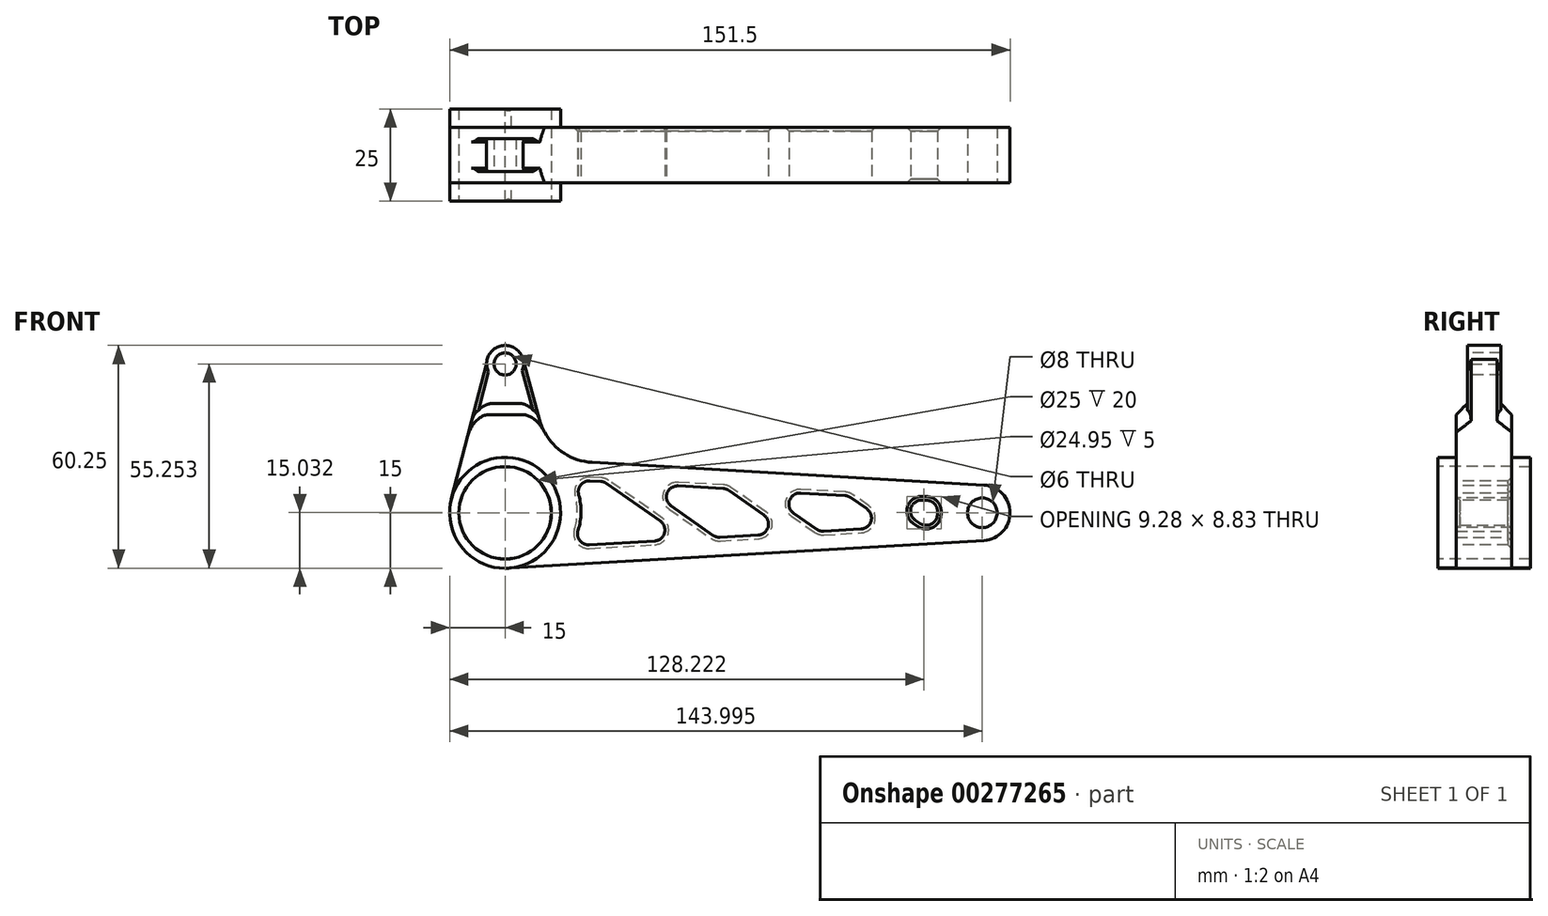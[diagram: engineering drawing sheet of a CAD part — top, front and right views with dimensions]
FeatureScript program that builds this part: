
annotation { "Feature Type Name" : "Feature", "Feature Type Description" : "" }
export const myFeature = defineFeature(function(context is Context, id is Id, definition is map)
    precondition{}
    {
        {
            var Q0;
            Q0=qCreatedBy(makeId("Front.planeOp"),FACE);
            var sketch = newSketch(context, id + "F0", { "sketchPlane" : qUnion([Q0])});
            skArc(sketch, "E0", {"start": v(129.43, -7.49) * mm, "mid": v(136.5, 0) * mm, "end": v(129.43, 7.49) * mm});
            skLineSegment(sketch, "E1", {"start": v(0, -15) * mm, "end": v(129.43, -7.49) * mm});
            skArc(sketch, "E2", {"start": v(4.84, 41.5) * mm, "mid": v(-0.62, 45.21) * mm, "end": v(-5, 40.25) * mm});
            skLineSegment(sketch, "E3", {"start": v(-5, 40.25) * mm, "end": v(-14.51, 3.79) * mm});
            skLineSegment(sketch, "E4", {"start": v(4.84, 41.5) * mm, "end": v(12.32, 14.29) * mm});
            skLineSegment(sketch, "E5.trimOffspring", {"start": v(12.32, 14.29) * mm, "end": v(129.43, 7.49) * mm});
            skPoint(sketch, "E6.start.orphan", {"position": v(0, 15) * mm});
            skArc(sketch, "E7.trimOffspring", {"start": v(-14.51, 3.79) * mm, "mid": v(-11.32, -9.84) * mm, "end": v(1.74, -14.9) * mm});
            skSolve(sketch);
        }
        {
            var Q0;
            {var subQ3=sQuery(id+"F0.wireOp",EDGE,"E0");Q0=makeQuery(id+"F0.imprint","IMPRINT",FACE,{"disambiguationData":[TD([[makeQuery(id+"F0.imprint","IMPRINT",EDGE,{"derivedFrom":subQ3}),1.0]])]});}
            extrude(context, id + "F1", {"entities" : qUnion([Q0]), "depth" : 15 * mm});
        }
        {
            var Q0;
            Q0=makeQuery(id+"F1.opExtrude","CAP_FACE",FACE,{"disambiguationData":[OSD([sQuery(id+"F0.wireOp",EDGE,"zeMrZWvo-Hzse-3JP0-Xgxd-alvhm16MrBRy"),sQuery(id+"F0.wireOp",EDGE,"E0"),sQuery(id+"F0.wireOp",EDGE,"E6"),sQuery(id+"F0.wireOp",EDGE,"E1")])],"isStart":false});
            var sketch = newSketch(context, id + "F2", { "sketchPlane" : qUnion([Q0])});
            skCircle(sketch, "E8", {"center": v(0, 0) * mm, "radius": 12.5 * mm});
            skCircle(sketch, "E9", {"center": v(129, 0) * mm, "radius": 4 * mm});
            skSolve(sketch);
        }
        {
            var Q0;
            Q0 = qSketchRegion(id + "F2", true);
            extrude(context, id + "F3", {"entities" : qUnion([Q0]), "operationType" : NewBodyOperationType.REMOVE, "endBound" : BoundingType.THROUGH_ALL, "oppositeDirection" : true, "depth" : 25 * mm});
        }
        {
            var Q0;
            Q0=makeQuery(id+"F1.opExtrude","CAP_FACE",FACE,{"disambiguationData":[OSD([sQuery(id+"F0.wireOp",EDGE,"zeMrZWvo-Hzse-3JP0-Xgxd-alvhm16MrBRy"),sQuery(id+"F0.wireOp",EDGE,"E0"),sQuery(id+"F0.wireOp",EDGE,"E6"),sQuery(id+"F0.wireOp",EDGE,"E1")])],"isStart":false});
            var sketch = newSketch(context, id + "F4", { "sketchPlane" : qUnion([Q0])});
            skLineSegment(sketch, "E10", {"start": v(18.1, 8.94) * mm, "end": v(26.69, 8.44) * mm});
            skLineSegment(sketch, "E11", {"start": v(17.63, -8.97) * mm, "end": v(49, -7.15) * mm});
            skArc(sketch, "E12", {"start": v(17.63, -8.97) * mm, "mid": v(20.5, -0.08) * mm, "end": v(18.1, 8.94) * mm});
            skArc(sketch, "E13", {"start": v(117.93, 3.15) * mm, "mid": v(116.86, 0.05) * mm, "end": v(117.46, -3.17) * mm});
            skLineSegment(sketch, "E14", {"start": v(26.69, 8.44) * mm, "end": v(49, -7.15) * mm});
            skLineSegment(sketch, "E15", {"start": v(36.2, 7.89) * mm, "end": v(57.06, -6.68) * mm});
            skLineSegment(sketch, "E16", {"start": v(59.79, 6.52) * mm, "end": v(77.02, -5.52) * mm});
            skLineSegment(sketch, "E17", {"start": v(69.3, 5.97) * mm, "end": v(85.08, -5.05) * mm});
            skLineSegment(sketch, "E18", {"start": v(92.66, 4.61) * mm, "end": v(104.85, -3.9) * mm});
            skLineSegment(sketch, "E19", {"start": v(102.18, 4.06) * mm, "end": v(112.91, -3.44) * mm});
            skLineSegment(sketch, "E20.trimOffspring", {"start": v(36.2, 7.89) * mm, "end": v(59.79, 6.52) * mm});
            skLineSegment(sketch, "E21.trimOffspring", {"start": v(57.06, -6.68) * mm, "end": v(77.02, -5.52) * mm});
            skLineSegment(sketch, "E22.trimOffspring", {"start": v(85.08, -5.05) * mm, "end": v(104.85, -3.9) * mm});
            skLineSegment(sketch, "E23.trimOffspring", {"start": v(69.3, 5.97) * mm, "end": v(92.66, 4.61) * mm});
            skLineSegment(sketch, "E24.trimOffspring", {"start": v(102.18, 4.06) * mm, "end": v(117.93, 3.15) * mm});
            skLineSegment(sketch, "E25.trimOffspring", {"start": v(112.91, -3.44) * mm, "end": v(117.46, -3.17) * mm});
            skSolve(sketch);
        }
        {
            var Q0;
            Q0 = qSketchRegion(id + "F4", true);
            extrude(context, id + "F5", {"entities" : qUnion([Q0]), "operationType" : NewBodyOperationType.REMOVE, "oppositeDirection" : true, "depth" : 25 * mm});
        }
        {
            var Q0;
            Q0=makeQuery(id+"F5.boolean.opBoolean","COPY",EDGE,{"derivedFrom":makeQuery(id+"F5.opExtrude","SWEPT_EDGE",EDGE,{"disambiguationData":[OSD([sQuery(id+"F4.wireOp",EDGE,"E10"),sQuery(id+"F4.wireOp",EDGE,"E12")])]})});
            var Q1;
            Q1=makeQuery(id+"F5.boolean.opBoolean","COPY",EDGE,{"derivedFrom":makeQuery(id+"F5.opExtrude","SWEPT_EDGE",EDGE,{"disambiguationData":[OSD([sQuery(id+"F4.wireOp",EDGE,"E11"),sQuery(id+"F4.wireOp",EDGE,"E12")])]})});
            var Q2;
            Q2=makeQuery(id+"F5.boolean.opBoolean","COPY",EDGE,{"derivedFrom":makeQuery(id+"F5.opExtrude","SWEPT_EDGE",EDGE,{"disambiguationData":[OSD([sQuery(id+"F4.wireOp",EDGE,"E10"),sQuery(id+"F4.wireOp",EDGE,"E14")])]})});
            var Q3;
            Q3=makeQuery(id+"F5.boolean.opBoolean","COPY",EDGE,{"derivedFrom":makeQuery(id+"F5.opExtrude","SWEPT_EDGE",EDGE,{"disambiguationData":[OSD([sQuery(id+"F4.wireOp",EDGE,"E11"),sQuery(id+"F4.wireOp",EDGE,"E14")])]})});
            var Q4;
            Q4=makeQuery(id+"F5.boolean.opBoolean","COPY",EDGE,{"derivedFrom":makeQuery(id+"F5.opExtrude","SWEPT_EDGE",EDGE,{"disambiguationData":[OSD([sQuery(id+"F4.wireOp",EDGE,"E15"),sQuery(id+"F4.wireOp",EDGE,"E21.trimOffspring")])]})});
            var Q5;
            Q5=makeQuery(id+"F5.boolean.opBoolean","COPY",EDGE,{"derivedFrom":makeQuery(id+"F5.opExtrude","SWEPT_EDGE",EDGE,{"disambiguationData":[OSD([sQuery(id+"F4.wireOp",EDGE,"E15"),sQuery(id+"F4.wireOp",EDGE,"E20.trimOffspring")])]})});
            var Q6;
            Q6=makeQuery(id+"F5.boolean.opBoolean","COPY",EDGE,{"derivedFrom":makeQuery(id+"F5.opExtrude","SWEPT_EDGE",EDGE,{"disambiguationData":[OSD([sQuery(id+"F4.wireOp",EDGE,"E16"),sQuery(id+"F4.wireOp",EDGE,"E20.trimOffspring")])]})});
            var Q7;
            Q7=makeQuery(id+"F5.boolean.opBoolean","COPY",EDGE,{"derivedFrom":makeQuery(id+"F5.opExtrude","SWEPT_EDGE",EDGE,{"disambiguationData":[OSD([sQuery(id+"F4.wireOp",EDGE,"E16"),sQuery(id+"F4.wireOp",EDGE,"E21.trimOffspring")])]})});
            var Q8;
            Q8=makeQuery(id+"F5.boolean.opBoolean","COPY",EDGE,{"derivedFrom":makeQuery(id+"F5.opExtrude","SWEPT_EDGE",EDGE,{"disambiguationData":[OSD([sQuery(id+"F4.wireOp",EDGE,"E17"),sQuery(id+"F4.wireOp",EDGE,"E23.trimOffspring")])]})});
            var Q9;
            Q9=makeQuery(id+"F5.boolean.opBoolean","COPY",EDGE,{"derivedFrom":makeQuery(id+"F5.opExtrude","SWEPT_EDGE",EDGE,{"disambiguationData":[OSD([sQuery(id+"F4.wireOp",EDGE,"E18"),sQuery(id+"F4.wireOp",EDGE,"E23.trimOffspring")])]})});
            var Q10;
            Q10=makeQuery(id+"F5.boolean.opBoolean","COPY",EDGE,{"derivedFrom":makeQuery(id+"F5.opExtrude","SWEPT_EDGE",EDGE,{"disambiguationData":[OSD([sQuery(id+"F4.wireOp",EDGE,"E18"),sQuery(id+"F4.wireOp",EDGE,"E22.trimOffspring")])]})});
            var Q11;
            Q11=makeQuery(id+"F5.boolean.opBoolean","COPY",EDGE,{"derivedFrom":makeQuery(id+"F5.opExtrude","SWEPT_EDGE",EDGE,{"disambiguationData":[OSD([sQuery(id+"F4.wireOp",EDGE,"E17"),sQuery(id+"F4.wireOp",EDGE,"E22.trimOffspring")])]})});
            var Q12;
            Q12=makeQuery(id+"F5.boolean.opBoolean","COPY",EDGE,{"derivedFrom":makeQuery(id+"F5.opExtrude","SWEPT_EDGE",EDGE,{"disambiguationData":[OSD([sQuery(id+"F4.wireOp",EDGE,"E19"),sQuery(id+"F4.wireOp",EDGE,"E24.trimOffspring")])]})});
            var Q13;
            Q13=makeQuery(id+"F5.boolean.opBoolean","COPY",EDGE,{"derivedFrom":makeQuery(id+"F5.opExtrude","SWEPT_EDGE",EDGE,{"disambiguationData":[OSD([sQuery(id+"F4.wireOp",EDGE,"E19"),sQuery(id+"F4.wireOp",EDGE,"E25.trimOffspring")])]})});
            var Q14;
            Q14=makeQuery(id+"F5.boolean.opBoolean","COPY",EDGE,{"derivedFrom":makeQuery(id+"F5.opExtrude","SWEPT_EDGE",EDGE,{"disambiguationData":[OSD([sQuery(id+"F4.wireOp",EDGE,"E13"),sQuery(id+"F4.wireOp",EDGE,"E25.trimOffspring")])]})});
            var Q15;
            Q15=makeQuery(id+"F5.boolean.opBoolean","COPY",EDGE,{"derivedFrom":makeQuery(id+"F5.opExtrude","SWEPT_EDGE",EDGE,{"disambiguationData":[OSD([sQuery(id+"F4.wireOp",EDGE,"E13"),sQuery(id+"F4.wireOp",EDGE,"E24.trimOffspring")])]})});
            fillet(context, id + "F6", {"entities" : qUnion([Q0, Q1, Q2, Q3, Q4, Q5, Q6, Q7, Q8, Q9, Q10, Q11, Q12, Q13, Q14, Q15]), "radius" : 3 * mm, "tangentPropagation" : true, "allowEdgeOverflow" : false});
        }
        {
            var Q0;
            Q0=makeQuery(id+"F1.opExtrude","CAP_FACE",FACE,{"disambiguationData":[OSD([sQuery(id+"F0.wireOp",EDGE,"zeMrZWvo-Hzse-3JP0-Xgxd-alvhm16MrBRy"),sQuery(id+"F0.wireOp",EDGE,"E0"),sQuery(id+"F0.wireOp",EDGE,"E6"),sQuery(id+"F0.wireOp",EDGE,"E1")])],"isStart":false});
            var sketch = newSketch(context, id + "F7", { "sketchPlane" : qUnion([Q0])});
            skCircle(sketch, "E26", {"center": v(0, 0) * mm, "radius": 15 * mm});
            skCircle(sketch, "E27", {"center": v(0, 0) * mm, "radius": 12.5 * mm});
            skSolve(sketch);
        }
        {
            var Q0;
            Q0 = qSketchRegion(id + "F7", true);
            extrude(context, id + "F8", {"entities" : qUnion([Q0]), "operationType" : NewBodyOperationType.ADD, "depth" : 5 * mm});
        }
        {
            var Q0;
            Q0=makeQuery(id+"F1.opExtrude","CAP_FACE",FACE,{"disambiguationData":[OSD([sQuery(id+"F0.wireOp",EDGE,"zeMrZWvo-Hzse-3JP0-Xgxd-alvhm16MrBRy"),sQuery(id+"F0.wireOp",EDGE,"E0"),sQuery(id+"F0.wireOp",EDGE,"E6"),sQuery(id+"F0.wireOp",EDGE,"E1")])],"isStart":true});
            var sketch = newSketch(context, id + "F9", { "sketchPlane" : qUnion([Q0])});
            skCircle(sketch, "E28", {"center": v(0, 0) * mm, "radius": 12.47 * mm});
            skCircle(sketch, "E29", {"center": v(0, 0) * mm, "radius": 15 * mm});
            skSolve(sketch);
        }
        {
            var Q0;
            Q0 = qSketchRegion(id + "F9", true);
            extrude(context, id + "F10", {"entities" : qUnion([Q0]), "operationType" : NewBodyOperationType.ADD, "depth" : 5 * mm});
        }
        {
            var Q0;
            Q0=makeQuery(id+"F5.boolean.opBoolean","COPY",EDGE,{"derivedFrom":makeQuery(id+"F5.opExtrude","CAP_EDGE",EDGE,{"disambiguationData":[OSD([sQuery(id+"F4.wireOp",EDGE,"E14")])],"isStart":true})});
            var Q1;
            Q1=makeQuery(id+"F5.boolean.opBoolean","COPY",EDGE,{"derivedFrom":makeQuery(id+"F5.opExtrude","CAP_EDGE",EDGE,{"disambiguationData":[OSD([sQuery(id+"F4.wireOp",EDGE,"E16")])],"isStart":true})});
            var Q2;
            Q2=makeQuery(id+"F5.boolean.opBoolean","COPY",EDGE,{"derivedFrom":makeQuery(id+"F5.opExtrude","CAP_EDGE",EDGE,{"disambiguationData":[OSD([sQuery(id+"F4.wireOp",EDGE,"E18")])],"isStart":true})});
            var Q3;
            Q3=makeQuery(id+"F6.opFillet","BLEND_EDGE",EDGE,{"blendedFrom":[makeQuery(id+"F5.boolean.opBoolean","COPY",EDGE,{"derivedFrom":makeQuery(id+"F5.opExtrude","SWEPT_EDGE",EDGE,{"disambiguationData":[OSD([sQuery(id+"F4.wireOp",EDGE,"E13"),sQuery(id+"F4.wireOp",EDGE,"E24.trimOffspring")])]})}),makeQuery(id+"F1.opExtrude","CAP_FACE",FACE,{"disambiguationData":[OSD([sQuery(id+"F0.wireOp",EDGE,"zeMrZWvo-Hzse-3JP0-Xgxd-alvhm16MrBRy"),sQuery(id+"F0.wireOp",EDGE,"E0"),sQuery(id+"F0.wireOp",EDGE,"E6"),sQuery(id+"F0.wireOp",EDGE,"E1")])],"isStart":false})],"blendedInto":[makeQuery(id+"F1.opExtrude","CAP_FACE",FACE,{"disambiguationData":[OSD([sQuery(id+"F0.wireOp",EDGE,"zeMrZWvo-Hzse-3JP0-Xgxd-alvhm16MrBRy"),sQuery(id+"F0.wireOp",EDGE,"E0"),sQuery(id+"F0.wireOp",EDGE,"E6"),sQuery(id+"F0.wireOp",EDGE,"E1")])],"isStart":false})]});
            var Q4;
            Q4=makeQuery(id+"F6.opFillet","BLEND_EDGE",EDGE,{"blendedFrom":[makeQuery(id+"F5.boolean.opBoolean","COPY",EDGE,{"derivedFrom":makeQuery(id+"F5.opExtrude","SWEPT_EDGE",EDGE,{"disambiguationData":[OSD([sQuery(id+"F4.wireOp",EDGE,"E19"),sQuery(id+"F4.wireOp",EDGE,"E24.trimOffspring")])]})}),makeQuery(id+"F1.opExtrude","CAP_FACE",FACE,{"disambiguationData":[OSD([sQuery(id+"F0.wireOp",EDGE,"zeMrZWvo-Hzse-3JP0-Xgxd-alvhm16MrBRy"),sQuery(id+"F0.wireOp",EDGE,"E0"),sQuery(id+"F0.wireOp",EDGE,"E6"),sQuery(id+"F0.wireOp",EDGE,"E1")])],"isStart":true})],"blendedInto":[makeQuery(id+"F1.opExtrude","CAP_FACE",FACE,{"disambiguationData":[OSD([sQuery(id+"F0.wireOp",EDGE,"zeMrZWvo-Hzse-3JP0-Xgxd-alvhm16MrBRy"),sQuery(id+"F0.wireOp",EDGE,"E0"),sQuery(id+"F0.wireOp",EDGE,"E6"),sQuery(id+"F0.wireOp",EDGE,"E1")])],"isStart":true})]});
            var Q5;
            Q5=makeQuery(id+"F5.boolean.opBoolean","INTERSECT",EDGE,{"derivedFrom":[makeQuery(id+"F1.opExtrude","CAP_FACE",FACE,{"disambiguationData":[OSD([sQuery(id+"F0.wireOp",EDGE,"zeMrZWvo-Hzse-3JP0-Xgxd-alvhm16MrBRy"),sQuery(id+"F0.wireOp",EDGE,"E0"),sQuery(id+"F0.wireOp",EDGE,"E6"),sQuery(id+"F0.wireOp",EDGE,"E1")])],"isStart":true}),makeQuery(id+"F5.opExtrude","SWEPT_FACE",FACE,{"disambiguationData":[OSD([sQuery(id+"F4.wireOp",EDGE,"E23.trimOffspring")])]})]});
            var Q6;
            Q6=makeQuery(id+"F5.boolean.opBoolean","INTERSECT",EDGE,{"derivedFrom":[makeQuery(id+"F1.opExtrude","CAP_FACE",FACE,{"disambiguationData":[OSD([sQuery(id+"F0.wireOp",EDGE,"zeMrZWvo-Hzse-3JP0-Xgxd-alvhm16MrBRy"),sQuery(id+"F0.wireOp",EDGE,"E0"),sQuery(id+"F0.wireOp",EDGE,"E6"),sQuery(id+"F0.wireOp",EDGE,"E1")])],"isStart":true}),makeQuery(id+"F5.opExtrude","SWEPT_FACE",FACE,{"disambiguationData":[OSD([sQuery(id+"F4.wireOp",EDGE,"E20.trimOffspring")])]})]});
            var Q7;
            Q7=makeQuery(id+"F5.boolean.opBoolean","INTERSECT",EDGE,{"derivedFrom":[makeQuery(id+"F1.opExtrude","CAP_FACE",FACE,{"disambiguationData":[OSD([sQuery(id+"F0.wireOp",EDGE,"zeMrZWvo-Hzse-3JP0-Xgxd-alvhm16MrBRy"),sQuery(id+"F0.wireOp",EDGE,"E0"),sQuery(id+"F0.wireOp",EDGE,"E6"),sQuery(id+"F0.wireOp",EDGE,"E1")])],"isStart":true}),makeQuery(id+"F5.opExtrude","SWEPT_FACE",FACE,{"disambiguationData":[OSD([sQuery(id+"F4.wireOp",EDGE,"E14")])]})]});
            chamfer(context, id + "F11", {"entities" : qUnion([Q0, Q1, Q2, Q3, Q4, Q5, Q6, Q7]), "width" : 1 * mm, "tangentPropagation" : true});
        }
        {
            var Q0;
            Q0=makeQuery(id+"F1.opExtrude","CAP_FACE",FACE,{"disambiguationData":[OSD([sQuery(id+"F0.wireOp",EDGE,"E0"),sQuery(id+"F0.wireOp",EDGE,"E1"),sQuery(id+"F0.wireOp",EDGE,"E2"),sQuery(id+"F0.wireOp",EDGE,"E3"),sQuery(id+"F0.wireOp",EDGE,"E4"),sQuery(id+"F0.wireOp",EDGE,"E5.trimOffspring"),sQuery(id+"F0.wireOp",EDGE,"E7.trimOffspring")])],"isStart":false});
            var sketch = newSketch(context, id + "F12", { "sketchPlane" : qUnion([Q0])});
            skCircle(sketch, "E30", {"center": v(0, 40.25) * mm, "radius": 3 * mm});
            skSolve(sketch);
        }
        {
            var Q0;
            Q0 = qSketchRegion(id + "F12", true);
            extrude(context, id + "F13", {"entities" : qUnion([Q0]), "operationType" : NewBodyOperationType.REMOVE, "oppositeDirection" : true, "depth" : 25 * mm});
        }
        {
            var Q0;
            Q0=makeQuery(id+"F1.opExtrude","SWEPT_EDGE",EDGE,{"disambiguationData":[OSD([sQuery(id+"F0.wireOp",EDGE,"E4"),sQuery(id+"F0.wireOp",EDGE,"E5.trimOffspring")])]});
            fillet(context, id + "F14", {"entities" : qUnion([Q0]), "radius" : 15.6 * mm, "tangentPropagation" : true, "allowEdgeOverflow" : false});
        }
        {
            var Q0;
            {var subQ0=sQuery(id+"F0.wireOp",EDGE,"E3");var subQ1=sQuery(id+"F0.wireOp",EDGE,"E7.trimOffspring");var subQ2=sQuery(id+"F0.wireOp",EDGE,"E1");var subQ3=sQuery(id+"F7.wireOp",EDGE,"E26");Q0=makeQuery(id+"F8.boolean.opBoolean","SPLIT",EDGE,{"disambiguationData":[TD([makeQuery(id+"F1.opExtrude","CAP_FACE",FACE,{"disambiguationData":[OSD([sQuery(id+"F0.wireOp",EDGE,"E0"),subQ2,sQuery(id+"F0.wireOp",EDGE,"E2"),subQ0,sQuery(id+"F0.wireOp",EDGE,"E4"),sQuery(id+"F0.wireOp",EDGE,"E5.trimOffspring"),subQ1])],"isStart":false}),makeQuery(id+"F1.opExtrude","SWEPT_FACE",FACE,{"disambiguationData":[OSD([subQ2])]}),makeQuery(id+"F1.opExtrude","SWEPT_FACE",FACE,{"disambiguationData":[OSD([subQ0])]}),makeQuery(id+"F1.opExtrude","SWEPT_FACE",FACE,{"disambiguationData":[OSD([subQ1])]}),makeQuery(id+"F8.opExtrude","SWEPT_FACE",FACE,{"disambiguationData":[OSD([subQ3])]}),makeQuery(id+"F8.opExtrude","CAP_FACE",FACE,{"disambiguationData":[OSD([subQ3,sQuery(id+"F7.wireOp",EDGE,"E27")])],"isStart":true})])],"derivedFrom":makeQuery(id+"F8.opExtrude","CAP_EDGE",EDGE,{"disambiguationData":[OSD([subQ3])],"isStart":true})});}
            var Q1;
            {var subQ0=sQuery(id+"F0.wireOp",EDGE,"E3");var subQ1=sQuery(id+"F0.wireOp",EDGE,"E7.trimOffspring");var subQ2=sQuery(id+"F0.wireOp",EDGE,"E1");var subQ3=sQuery(id+"F9.wireOp",EDGE,"E29");Q1=makeQuery(id+"F10.boolean.opBoolean","SPLIT",EDGE,{"disambiguationData":[TD([makeQuery(id+"F1.opExtrude","CAP_FACE",FACE,{"disambiguationData":[OSD([sQuery(id+"F0.wireOp",EDGE,"E0"),subQ2,sQuery(id+"F0.wireOp",EDGE,"E2"),subQ0,sQuery(id+"F0.wireOp",EDGE,"E4"),sQuery(id+"F0.wireOp",EDGE,"E5.trimOffspring"),subQ1])],"isStart":true}),makeQuery(id+"F1.opExtrude","SWEPT_FACE",FACE,{"disambiguationData":[OSD([subQ2])]}),makeQuery(id+"F1.opExtrude","SWEPT_FACE",FACE,{"disambiguationData":[OSD([subQ0])]}),makeQuery(id+"F1.opExtrude","SWEPT_FACE",FACE,{"disambiguationData":[OSD([subQ1])]}),makeQuery(id+"F8.opExtrude","SWEPT_FACE",FACE,{"disambiguationData":[OSD([sQuery(id+"F7.wireOp",EDGE,"E26")])]}),makeQuery(id+"F10.opExtrude","CAP_FACE",FACE,{"disambiguationData":[OSD([sQuery(id+"F9.wireOp",EDGE,"E28"),subQ3])],"isStart":true}),makeQuery(id+"F10.opExtrude","SWEPT_FACE",FACE,{"disambiguationData":[OSD([subQ3])]})])],"derivedFrom":makeQuery(id+"F10.opExtrude","CAP_EDGE",EDGE,{"disambiguationData":[OSD([subQ3])],"isStart":true})});}
            fillet(context, id + "F15", {"entities" : qUnion([Q0, Q1]), "radius" : 5 * mm, "tangentPropagation" : true, "allowEdgeOverflow" : false});
        }
        {
            var Q0;
            Q0=qCreatedBy(makeId("Right.planeOp"),FACE);
            var sketch = newSketch(context, id + "F16", { "sketchPlane" : qUnion([Q0])});
            skLineSegment(sketch, "E31.bottom", {"start": v(-22.36, 47.16) * mm, "end": v(-12, 47.16) * mm});
            skLineSegment(sketch, "E31.top", {"start": v(-22.36, 24.54) * mm, "end": v(-12, 24.54) * mm});
            skLineSegment(sketch, "E31.left", {"start": v(-22.36, 47.16) * mm, "end": v(-22.36, 24.54) * mm});
            skLineSegment(sketch, "E31.right", {"start": v(-12, 47.16) * mm, "end": v(-12, 24.54) * mm});
            skLineSegment(sketch, "E32.bottom", {"start": v(-3, 47.16) * mm, "end": v(3.68, 47.16) * mm});
            skLineSegment(sketch, "E32.top", {"start": v(-3, 24.54) * mm, "end": v(3.68, 24.54) * mm});
            skLineSegment(sketch, "E32.left", {"start": v(-3, 47.16) * mm, "end": v(-3, 24.54) * mm});
            skLineSegment(sketch, "E32.right", {"start": v(3.68, 47.16) * mm, "end": v(3.68, 24.54) * mm});
            skSolve(sketch);
        }
        {
            var Q0;
            Q0 = qSketchRegion(id + "F16", true);
            extrude(context, id + "F17", {"entities" : qUnion([Q0]), "operationType" : NewBodyOperationType.REMOVE, "endBound" : BoundingType.THROUGH_ALL, "oppositeDirection" : true, "depth" : 25 * mm, "hasSecondDirection" : true, "secondDirectionBound" : SecondDirectionBoundingType.THROUGH_ALL, "secondDirectionOppositeDirection" : false, "secondDirectionDepth" : 25 * mm});
        }
        {
            var Q0;
            Q0=makeQuery(id+"F17.boolean.opBoolean","COPY",EDGE,{"derivedFrom":makeQuery(id+"F17.opExtrude","SWEPT_EDGE",EDGE,{"disambiguationData":[OSD([sQuery(id+"F16.wireOp",EDGE,"E31.top"),sQuery(id+"F16.wireOp",EDGE,"E31.right")])]})});
            var Q1;
            Q1=makeQuery(id+"F17.boolean.opBoolean","COPY",EDGE,{"derivedFrom":makeQuery(id+"F17.opExtrude","SWEPT_EDGE",EDGE,{"disambiguationData":[OSD([sQuery(id+"F16.wireOp",EDGE,"E32.top"),sQuery(id+"F16.wireOp",EDGE,"E32.left")])]})});
            chamfer(context, id + "F18", {"entities" : qUnion([Q0, Q1]), "width" : 5 * mm, "tangentPropagation" : true});
        }
        {
            var Q0;
            Q0=makeQuery(id+"F18.opChamfer","BLEND_EDGE",EDGE,{"blendedFrom":[makeQuery(id+"F17.boolean.opBoolean","COPY",EDGE,{"derivedFrom":makeQuery(id+"F17.opExtrude","SWEPT_EDGE",EDGE,{"disambiguationData":[OSD([sQuery(id+"F16.wireOp",EDGE,"E31.top"),sQuery(id+"F16.wireOp",EDGE,"E31.right")])]})}),makeQuery(id+"F1.opExtrude","SWEPT_FACE",FACE,{"disambiguationData":[OSD([sQuery(id+"F0.wireOp",EDGE,"E3")])]})],"blendedInto":[makeQuery(id+"F1.opExtrude","SWEPT_FACE",FACE,{"disambiguationData":[OSD([sQuery(id+"F0.wireOp",EDGE,"E3")])]})]});
            var Q1;
            Q1=makeQuery(id+"F18.opChamfer","BLEND_EDGE",EDGE,{"blendedFrom":[makeQuery(id+"F17.boolean.opBoolean","COPY",EDGE,{"derivedFrom":makeQuery(id+"F17.opExtrude","SWEPT_EDGE",EDGE,{"disambiguationData":[OSD([sQuery(id+"F16.wireOp",EDGE,"E31.top"),sQuery(id+"F16.wireOp",EDGE,"E31.right")])]})}),makeQuery(id+"F1.opExtrude","SWEPT_FACE",FACE,{"disambiguationData":[OSD([sQuery(id+"F0.wireOp",EDGE,"E4")])]})],"blendedInto":[makeQuery(id+"F1.opExtrude","SWEPT_FACE",FACE,{"disambiguationData":[OSD([sQuery(id+"F0.wireOp",EDGE,"E4")])]})]});
            var Q2;
            Q2=makeQuery(id+"F18.opChamfer","BLEND_EDGE",EDGE,{"blendedFrom":[makeQuery(id+"F17.boolean.opBoolean","COPY",EDGE,{"derivedFrom":makeQuery(id+"F17.opExtrude","SWEPT_EDGE",EDGE,{"disambiguationData":[OSD([sQuery(id+"F16.wireOp",EDGE,"E32.top"),sQuery(id+"F16.wireOp",EDGE,"E32.left")])]})}),makeQuery(id+"F1.opExtrude","SWEPT_FACE",FACE,{"disambiguationData":[OSD([sQuery(id+"F0.wireOp",EDGE,"E4")])]})],"blendedInto":[makeQuery(id+"F1.opExtrude","SWEPT_FACE",FACE,{"disambiguationData":[OSD([sQuery(id+"F0.wireOp",EDGE,"E4")])]})]});
            var Q3;
            Q3=makeQuery(id+"F18.opChamfer","BLEND_EDGE",EDGE,{"blendedFrom":[makeQuery(id+"F17.boolean.opBoolean","COPY",EDGE,{"derivedFrom":makeQuery(id+"F17.opExtrude","SWEPT_EDGE",EDGE,{"disambiguationData":[OSD([sQuery(id+"F16.wireOp",EDGE,"E32.top"),sQuery(id+"F16.wireOp",EDGE,"E32.left")])]})}),makeQuery(id+"F1.opExtrude","SWEPT_FACE",FACE,{"disambiguationData":[OSD([sQuery(id+"F0.wireOp",EDGE,"E3")])]})],"blendedInto":[makeQuery(id+"F1.opExtrude","SWEPT_FACE",FACE,{"disambiguationData":[OSD([sQuery(id+"F0.wireOp",EDGE,"E3")])]})]});
            fillet(context, id + "F19", {"entities" : qUnion([Q0, Q1, Q2, Q3]), "radius" : 5 * mm, "tangentPropagation" : true, "allowEdgeOverflow" : false});
        }
        {
            var Q0;
            Q0=makeQuery(id+"F17.boolean.opBoolean","INTERSECT",EDGE,{"derivedFrom":[makeQuery(id+"F1.opExtrude","SWEPT_FACE",FACE,{"disambiguationData":[OSD([sQuery(id+"F0.wireOp",EDGE,"E4")])]}),makeQuery(id+"F17.opExtrude","SWEPT_FACE",FACE,{"disambiguationData":[OSD([sQuery(id+"F16.wireOp",EDGE,"E32.left")])]})]});
            var Q1;
            Q1=makeQuery(id+"F17.boolean.opBoolean","INTERSECT",EDGE,{"derivedFrom":[makeQuery(id+"F1.opExtrude","SWEPT_FACE",FACE,{"disambiguationData":[OSD([sQuery(id+"F0.wireOp",EDGE,"E4")])]}),makeQuery(id+"F17.opExtrude","SWEPT_FACE",FACE,{"disambiguationData":[OSD([sQuery(id+"F16.wireOp",EDGE,"E31.right")])]})]});
            var Q2;
            Q2=makeQuery(id+"F17.boolean.opBoolean","INTERSECT",EDGE,{"derivedFrom":[makeQuery(id+"F1.opExtrude","SWEPT_FACE",FACE,{"disambiguationData":[OSD([sQuery(id+"F0.wireOp",EDGE,"E3")])]}),makeQuery(id+"F17.opExtrude","SWEPT_FACE",FACE,{"disambiguationData":[OSD([sQuery(id+"F16.wireOp",EDGE,"E31.right")])]})]});
            var Q3;
            Q3=makeQuery(id+"F17.boolean.opBoolean","INTERSECT",EDGE,{"derivedFrom":[makeQuery(id+"F1.opExtrude","SWEPT_FACE",FACE,{"disambiguationData":[OSD([sQuery(id+"F0.wireOp",EDGE,"E3")])]}),makeQuery(id+"F17.opExtrude","SWEPT_FACE",FACE,{"disambiguationData":[OSD([sQuery(id+"F16.wireOp",EDGE,"E32.left")])]})]});
            chamfer(context, id + "F20", {"entities" : qUnion([Q0, Q1, Q2, Q3]), "width" : 1 * mm, "tangentPropagation" : true});
        }
    });
